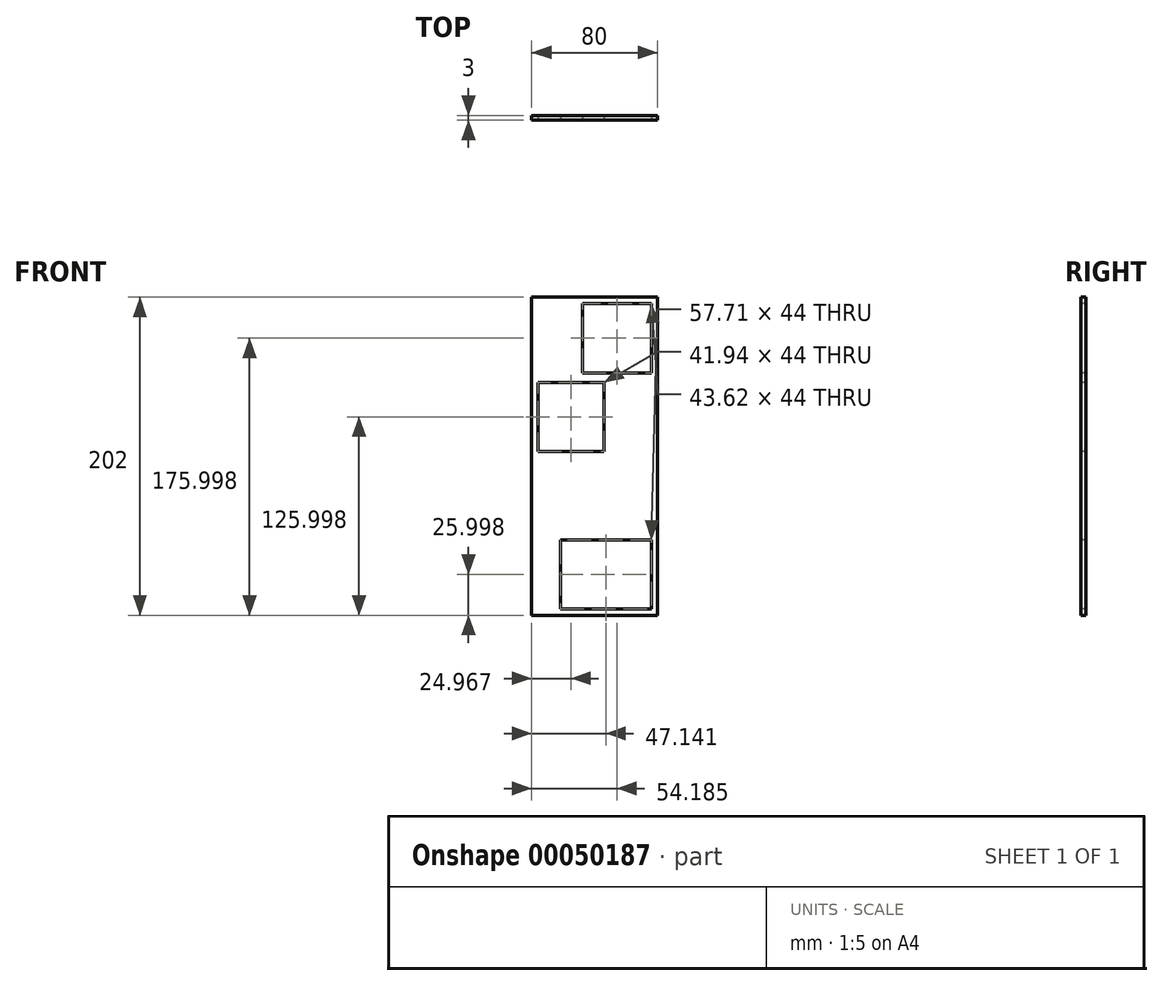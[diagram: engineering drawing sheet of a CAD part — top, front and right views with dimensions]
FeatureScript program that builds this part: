
annotation { "Feature Type Name" : "Feature", "Feature Type Description" : "" }
export const myFeature = defineFeature(function(context is Context, id is Id, definition is map)
    precondition{}
    {
        {
            var Q0;
            Q0=qCreatedBy(makeId("Front.planeOp"),FACE);
            var sketch = newSketch(context, id + "F0", { "sketchPlane" : qUnion([Q0])});
            skLineSegment(sketch, "E0.bottom", {"start": v(-59.74, 128.88) * mm, "end": v(20.26, 128.88) * mm});
            skLineSegment(sketch, "E0.top", {"start": v(-59.74, -73.12) * mm, "end": v(20.26, -73.12) * mm});
            skLineSegment(sketch, "E0.left", {"start": v(-59.74, 128.88) * mm, "end": v(-59.74, -73.12) * mm});
            skLineSegment(sketch, "E0.right", {"start": v(20.26, 128.88) * mm, "end": v(20.26, -73.12) * mm});
            skSolve(sketch);
        }
        {
            var Q0;
            Q0 = qSketchRegion(id + "F0", true);
            extrude(context, id + "F1", {"entities" : qUnion([Q0]), "depth" : 3 * mm});
        }
        {
            var Q0;
            Q0=makeQuery(id+"F1.opExtrude","CAP_FACE",FACE,{"disambiguationData":[OSD([sQuery(id+"F0.wireOp",EDGE,"E0.bottom"),sQuery(id+"F0.wireOp",EDGE,"E0.top"),sQuery(id+"F0.wireOp",EDGE,"E0.left"),sQuery(id+"F0.wireOp",EDGE,"E0.right")])],"isStart":false});
            var sketch = newSketch(context, id + "F2", { "sketchPlane" : qUnion([Q0])});
            skLineSegment(sketch, "E1.bottom", {"start": v(-59.74, 128.88) * mm, "end": v(20.26, 128.88) * mm});
            skLineSegment(sketch, "E1.top", {"start": v(-59.74, -73.12) * mm, "end": v(20.26, -73.12) * mm});
            skLineSegment(sketch, "E1.left", {"start": v(-59.74, 128.88) * mm, "end": v(-59.74, -73.12) * mm});
            skLineSegment(sketch, "E1.right", {"start": v(20.26, 128.88) * mm, "end": v(20.26, -73.12) * mm});
            skLineSegment(sketch, "E2.0", {"start": v(-57.74, 126.88) * mm, "end": v(18.26, 126.88) * mm});
            skLineSegment(sketch, "E2.1", {"start": v(-57.74, 126.88) * mm, "end": v(-57.74, -71.12) * mm});
            skLineSegment(sketch, "E2.2", {"start": v(-57.74, -71.12) * mm, "end": v(18.26, -71.12) * mm});
            skLineSegment(sketch, "E2.3", {"start": v(18.26, 126.88) * mm, "end": v(18.26, -71.12) * mm});
            skPoint(sketch, "E3.start.orphan", {"position": v(-19.74, -71.12) * mm});
            skLineSegment(sketch, "E4.top", {"start": v(18.26, -71.12) * mm, "end": v(-43.45, -71.12) * mm});
            skLineSegment(sketch, "E4.left", {"start": v(18.26, -23.12) * mm, "end": v(18.26, -71.12) * mm});
            skLineSegment(sketch, "E5.right", {"start": v(-57.74, 28.88) * mm, "end": v(-57.74, 76.88) * mm});
            skLineSegment(sketch, "E6", {"start": v(-43.45, -42.18) * mm, "end": v(-41.45, -42.18) * mm});
            skLineSegment(sketch, "E7.bottom", {"start": v(-41.45, -25.12) * mm, "end": v(16.26, -25.12) * mm});
            skLineSegment(sketch, "E7.top", {"start": v(-41.45, -69.12) * mm, "end": v(16.26, -69.12) * mm});
            skLineSegment(sketch, "E7.left", {"start": v(-41.45, -25.12) * mm, "end": v(-41.45, -69.12) * mm});
            skLineSegment(sketch, "E7.right", {"start": v(16.26, -25.12) * mm, "end": v(16.26, -69.12) * mm});
            skPoint(sketch, "E8.end.orphan", {"position": v(-12.6, -69.12) * mm});
            skPoint(sketch, "E8.start.orphan", {"position": v(-12.6, -71.12) * mm});
            skPoint(sketch, "E9.end.orphan", {"position": v(16.26, -42.68) * mm});
            skPoint(sketch, "E10.end.orphan", {"position": v(-19.74, -25.12) * mm});
            skPoint(sketch, "E11.start.orphan", {"position": v(-19.74, -23.12) * mm});
            skLineSegment(sketch, "E12.bottom", {"start": v(-55.74, 74.88) * mm, "end": v(-13.8, 74.88) * mm});
            skLineSegment(sketch, "E12.top", {"start": v(-55.74, 30.88) * mm, "end": v(-13.8, 30.88) * mm});
            skLineSegment(sketch, "E12.left", {"start": v(-55.74, 74.88) * mm, "end": v(-55.74, 30.88) * mm});
            skLineSegment(sketch, "E12.right", {"start": v(-13.8, 74.88) * mm, "end": v(-13.8, 30.88) * mm});
            skPoint(sketch, "E13.orphan", {"position": v(-11.8, 28.88) * mm});
            skPoint(sketch, "E14.end.orphan", {"position": v(-38.4, 30.88) * mm});
            skPoint(sketch, "E15.end.orphan", {"position": v(-55.74, 55.9) * mm});
            skPoint(sketch, "E16.end.orphan", {"position": v(-13.8, 51.95) * mm});
            skPoint(sketch, "E17.end.orphan", {"position": v(-19.74, 28.88) * mm});
            skPoint(sketch, "E18.end.orphan", {"position": v(-19.74, 74.88) * mm});
            skPoint(sketch, "E19.end.orphan", {"position": v(-19.74, 78.88) * mm});
            skPoint(sketch, "E19.start.orphan", {"position": v(-19.74, 76.88) * mm});
            skLineSegment(sketch, "E20.bottom", {"start": v(-27.37, 124.88) * mm, "end": v(16.26, 124.88) * mm});
            skLineSegment(sketch, "E20.top", {"start": v(-27.37, 80.88) * mm, "end": v(16.26, 80.88) * mm});
            skLineSegment(sketch, "E20.left", {"start": v(-27.37, 124.88) * mm, "end": v(-27.37, 80.88) * mm});
            skLineSegment(sketch, "E20.right", {"start": v(16.26, 124.88) * mm, "end": v(16.26, 80.88) * mm});
            skPoint(sketch, "E21.end.orphan", {"position": v(-3.38, 124.88) * mm});
            skPoint(sketch, "E22.end.orphan", {"position": v(16.26, 107.55) * mm});
            skPoint(sketch, "E23.end.orphan", {"position": v(-6.54, 80.88) * mm});
            skPoint(sketch, "E24.right.end.orphan", {"position": v(-29.37, 78.88) * mm});
            skPoint(sketch, "E25.end.orphan", {"position": v(-27.37, 103.86) * mm});
            skSolve(sketch);
        }
        {
            var Q0;
            Q0=makeQuery(id+"F2.imprint","IMPRINT",FACE,{"disambiguationData":[TD([[makeQuery(id+"F2.imprint","IMPRINT",EDGE,{"derivedFrom":sQuery(id+"F2.wireOp",EDGE,"E12.bottom")}),-1.0]])]});
            var Q1;
            Q1=makeQuery(id+"F2.imprint","IMPRINT",FACE,{"disambiguationData":[TD([[makeQuery(id+"F2.imprint","IMPRINT",EDGE,{"derivedFrom":sQuery(id+"F2.wireOp",EDGE,"E20.bottom")}),-1.0]])]});
            var Q2;
            {var subQ3=sQuery(id+"F2.wireOp",EDGE,"E7.bottom");Q2=makeQuery(id+"F2.imprint","IMPRINT",FACE,{"disambiguationData":[TD([[makeQuery(id+"F2.imprint","IMPRINT",EDGE,{"derivedFrom":subQ3}),-1.0]])]});}
            extrude(context, id + "F3", {"entities" : qUnion([Q0, Q1, Q2]), "operationType" : NewBodyOperationType.REMOVE, "oppositeDirection" : true, "depth" : 25 * mm});
        }
    });
